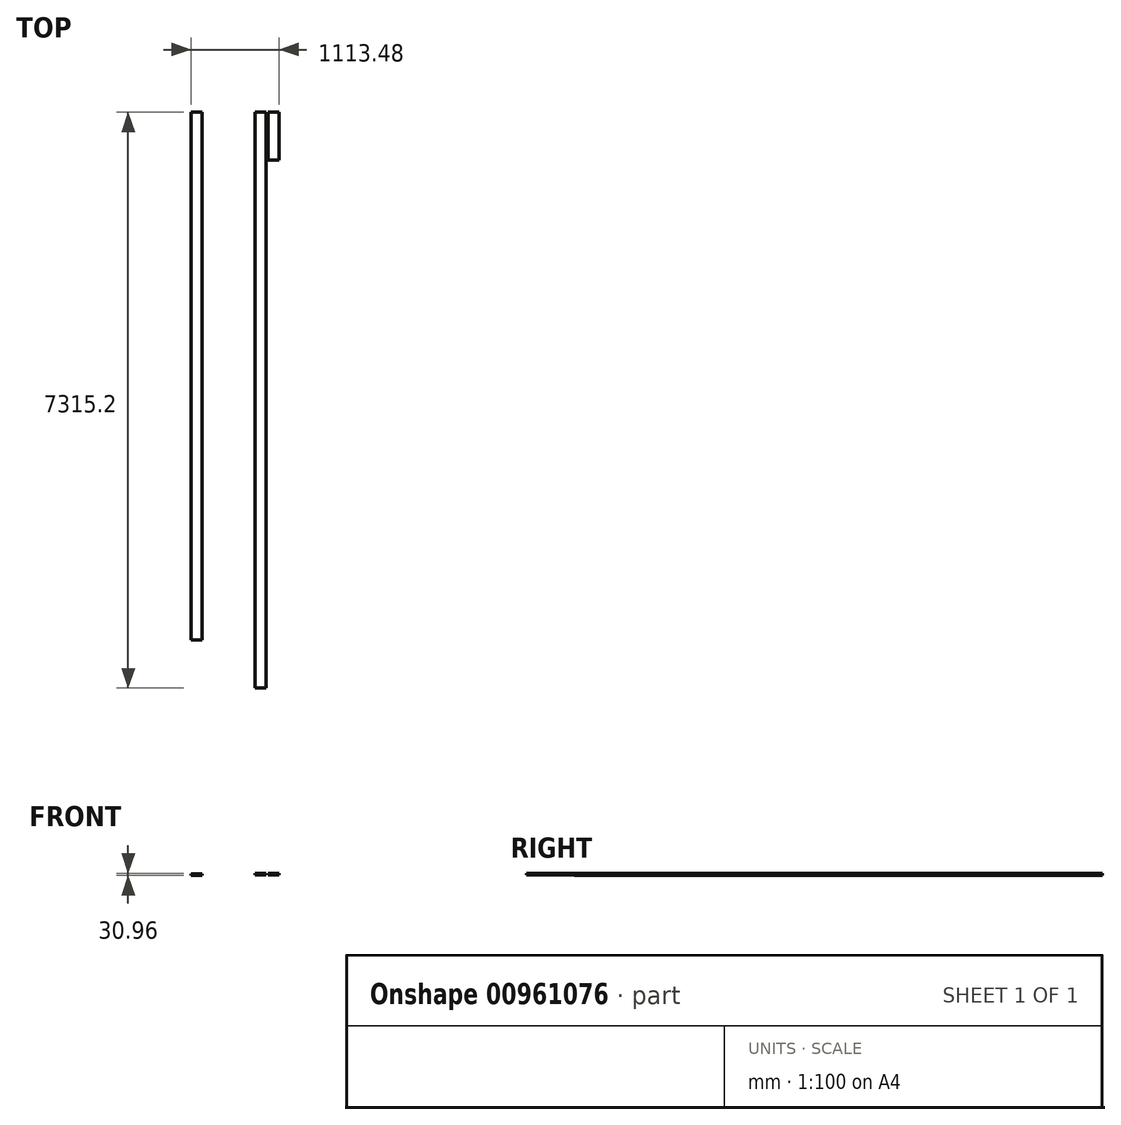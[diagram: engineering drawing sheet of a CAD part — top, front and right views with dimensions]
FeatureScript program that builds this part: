
annotation { "Feature Type Name" : "Feature", "Feature Type Description" : "" }
export const myFeature = defineFeature(function(context is Context, id is Id, definition is map)
    precondition{}
    {
        {
            var Q0;
            Q0=qCreatedBy(makeId("Front.planeOp"),FACE);
            var sketch = newSketch(context, id + "F0", { "sketchPlane" : qUnion([Q0])});
            skLineSegment(sketch, "E0.bottom", {"start": v(-146.06, 12.17) * mm, "end": v(-6.36, 12.17) * mm});
            skLineSegment(sketch, "E0.top", {"start": v(-146.06, -11.7) * mm, "end": v(-6.36, -11.7) * mm});
            skLineSegment(sketch, "E0.left", {"start": v(-146.06, 12.17) * mm, "end": v(-146.06, -11.7) * mm});
            skLineSegment(sketch, "E0.right", {"start": v(-6.36, 12.17) * mm, "end": v(-6.36, -11.7) * mm});
            skLineSegment(sketch, "E1.bottom", {"start": v(15.3, 12.22) * mm, "end": v(155, 12.22) * mm});
            skLineSegment(sketch, "E1.top", {"start": v(15.3, -11.66) * mm, "end": v(155, -11.66) * mm});
            skLineSegment(sketch, "E1.left", {"start": v(15.3, 12.22) * mm, "end": v(15.3, -11.66) * mm});
            skLineSegment(sketch, "E1.right", {"start": v(155, 12.22) * mm, "end": v(155, -11.66) * mm});
            skSolve(sketch);
        }
        {
            var Q0;
            Q0=qCreatedBy(makeId("Front.planeOp"),FACE);
            var sketch = newSketch(context, id + "F1", { "sketchPlane" : qUnion([Q0])});
            skLineSegment(sketch, "E2.bottom", {"start": v(-818.78, 4.12) * mm, "end": v(-958.48, 4.12) * mm});
            skLineSegment(sketch, "E2.top", {"start": v(-818.78, -18.74) * mm, "end": v(-958.48, -18.74) * mm});
            skLineSegment(sketch, "E2.left", {"start": v(-818.78, 4.12) * mm, "end": v(-818.78, -18.74) * mm});
            skLineSegment(sketch, "E2.right", {"start": v(-958.48, 4.12) * mm, "end": v(-958.48, -18.74) * mm});
            skPoint(sketch, "E2.middle", {"position": v(-888.63, -7.31) * mm});
            skLineSegment(sketch, "E3.1.0.0", {"start": v(-823.6, 4.12) * mm, "end": v(-823.6, -18.74) * mm});
            skLineSegment(sketch, "E3.1.0.1", {"start": v(-683.9, 4.12) * mm, "end": v(-823.6, 4.12) * mm});
            skLineSegment(sketch, "E3.1.0.2", {"start": v(-683.9, -18.74) * mm, "end": v(-823.6, -18.74) * mm});
            skLineSegment(sketch, "E3.1.0.3", {"start": v(-683.9, 4.12) * mm, "end": v(-683.9, -18.74) * mm});
            skLineSegment(sketch, "E3.2.0.0", {"start": v(-688.74, 4.12) * mm, "end": v(-688.74, -18.74) * mm});
            skLineSegment(sketch, "E3.2.0.1", {"start": v(-549.04, 4.12) * mm, "end": v(-688.74, 4.12) * mm});
            skLineSegment(sketch, "E3.2.0.2", {"start": v(-549.04, -18.74) * mm, "end": v(-688.74, -18.74) * mm});
            skLineSegment(sketch, "E3.2.0.3", {"start": v(-549.04, 4.12) * mm, "end": v(-549.04, -18.74) * mm});
            skLineSegment(sketch, "E3.3.0.0", {"start": v(-553.86, 4.12) * mm, "end": v(-553.86, -18.74) * mm});
            skLineSegment(sketch, "E3.3.0.1", {"start": v(-414.16, 4.12) * mm, "end": v(-553.86, 4.12) * mm});
            skLineSegment(sketch, "E3.3.0.2", {"start": v(-414.16, -18.74) * mm, "end": v(-553.86, -18.74) * mm});
            skLineSegment(sketch, "E3.3.0.3", {"start": v(-414.16, 4.12) * mm, "end": v(-414.16, -18.74) * mm});
            skLineSegment(sketch, "E3.4.0.0", {"start": v(-418.99, 4.12) * mm, "end": v(-418.99, -18.74) * mm});
            skLineSegment(sketch, "E3.4.0.1", {"start": v(-279.29, 4.12) * mm, "end": v(-418.99, 4.12) * mm});
            skLineSegment(sketch, "E3.4.0.2", {"start": v(-279.29, -18.74) * mm, "end": v(-418.99, -18.74) * mm});
            skLineSegment(sketch, "E3.4.0.3", {"start": v(-279.29, 4.12) * mm, "end": v(-279.29, -18.74) * mm});
            skLineSegment(sketch, "E3.5.0.0", {"start": v(-284.11, 4.12) * mm, "end": v(-284.11, -18.74) * mm});
            skLineSegment(sketch, "E3.5.0.1", {"start": v(-144.41, 4.12) * mm, "end": v(-284.11, 4.12) * mm});
            skLineSegment(sketch, "E3.5.0.2", {"start": v(-144.41, -18.74) * mm, "end": v(-284.11, -18.74) * mm});
            skLineSegment(sketch, "E3.5.0.3", {"start": v(-144.41, 4.12) * mm, "end": v(-144.41, -18.74) * mm});
            skLineSegment(sketch, "E3.direction1", {"start": v(-958.48, -18.74) * mm, "end": v(-823.6, -18.74) * mm, "construction": true});
            skLineSegment(sketch, "E4.0.6.0", {"start": v(-149.24, 4.12) * mm, "end": v(-149.24, -18.74) * mm});
            skLineSegment(sketch, "E4.3.6.0", {"start": v(-9.54, 4.12) * mm, "end": v(-149.24, 4.12) * mm});
            skLineSegment(sketch, "E4.6.6.0", {"start": v(-9.54, -18.74) * mm, "end": v(-149.24, -18.74) * mm});
            skLineSegment(sketch, "E4.9.6.0", {"start": v(-9.54, 4.12) * mm, "end": v(-9.54, -18.74) * mm});
            skLineSegment(sketch, "E4.0.7.0", {"start": v(-14.37, 4.12) * mm, "end": v(-14.37, -18.74) * mm});
            skLineSegment(sketch, "E4.3.7.0", {"start": v(125.33, 4.12) * mm, "end": v(-14.37, 4.12) * mm});
            skLineSegment(sketch, "E4.6.7.0", {"start": v(125.33, -18.74) * mm, "end": v(-14.37, -18.74) * mm});
            skLineSegment(sketch, "E4.9.7.0", {"start": v(125.33, 4.12) * mm, "end": v(125.33, -18.74) * mm});
            skLineSegment(sketch, "E4.0.8.0", {"start": v(120.5, 4.12) * mm, "end": v(120.5, -18.74) * mm});
            skLineSegment(sketch, "E4.3.8.0", {"start": v(260.2, 4.12) * mm, "end": v(120.5, 4.12) * mm});
            skLineSegment(sketch, "E4.6.8.0", {"start": v(260.2, -18.74) * mm, "end": v(120.5, -18.74) * mm});
            skLineSegment(sketch, "E4.9.8.0", {"start": v(260.2, 4.12) * mm, "end": v(260.2, -18.74) * mm});
            skLineSegment(sketch, "E4.0.9.0", {"start": v(255.38, 4.12) * mm, "end": v(255.38, -18.74) * mm});
            skLineSegment(sketch, "E4.3.9.0", {"start": v(395.08, 4.12) * mm, "end": v(255.38, 4.12) * mm});
            skLineSegment(sketch, "E4.6.9.0", {"start": v(395.08, -18.74) * mm, "end": v(255.38, -18.74) * mm});
            skLineSegment(sketch, "E4.9.9.0", {"start": v(395.08, 4.12) * mm, "end": v(395.08, -18.74) * mm});
            skLineSegment(sketch, "E5.0.10.0", {"start": v(390.26, 4.12) * mm, "end": v(390.26, -18.74) * mm});
            skLineSegment(sketch, "E5.3.10.0", {"start": v(529.96, 4.12) * mm, "end": v(390.26, 4.12) * mm});
            skLineSegment(sketch, "E5.6.10.0", {"start": v(529.96, -18.74) * mm, "end": v(390.26, -18.74) * mm});
            skLineSegment(sketch, "E5.9.10.0", {"start": v(529.96, 4.12) * mm, "end": v(529.96, -18.74) * mm});
            skLineSegment(sketch, "E5.0.11.0", {"start": v(525.13, 4.12) * mm, "end": v(525.13, -18.74) * mm});
            skLineSegment(sketch, "E5.3.11.0", {"start": v(664.83, 4.12) * mm, "end": v(525.13, 4.12) * mm});
            skLineSegment(sketch, "E5.6.11.0", {"start": v(664.83, -18.74) * mm, "end": v(525.13, -18.74) * mm});
            skLineSegment(sketch, "E5.9.11.0", {"start": v(664.83, 4.12) * mm, "end": v(664.83, -18.74) * mm});
            skLineSegment(sketch, "E5.0.12.0", {"start": v(660, 4.12) * mm, "end": v(660, -18.74) * mm});
            skLineSegment(sketch, "E5.3.12.0", {"start": v(799.7, 4.12) * mm, "end": v(660, 4.12) * mm});
            skLineSegment(sketch, "E5.6.12.0", {"start": v(799.7, -18.74) * mm, "end": v(660, -18.74) * mm});
            skLineSegment(sketch, "E5.9.12.0", {"start": v(799.7, 4.12) * mm, "end": v(799.7, -18.74) * mm});
            skLineSegment(sketch, "E5.0.13.0", {"start": v(794.88, 4.12) * mm, "end": v(794.88, -18.74) * mm});
            skLineSegment(sketch, "E5.3.13.0", {"start": v(934.58, 4.12) * mm, "end": v(794.88, 4.12) * mm});
            skLineSegment(sketch, "E5.6.13.0", {"start": v(934.58, -18.74) * mm, "end": v(794.88, -18.74) * mm});
            skLineSegment(sketch, "E5.9.13.0", {"start": v(934.58, 4.12) * mm, "end": v(934.58, -18.74) * mm});
            skLineSegment(sketch, "E5.0.14.0", {"start": v(929.75, 4.12) * mm, "end": v(929.75, -18.74) * mm});
            skLineSegment(sketch, "E5.3.14.0", {"start": v(1069.45, 4.12) * mm, "end": v(929.75, 4.12) * mm});
            skLineSegment(sketch, "E5.6.14.0", {"start": v(1069.45, -18.74) * mm, "end": v(929.75, -18.74) * mm});
            skLineSegment(sketch, "E5.9.14.0", {"start": v(1069.45, 4.12) * mm, "end": v(1069.45, -18.74) * mm});
            skSolve(sketch);
        }
        {
            var Q0;
            Q0=makeQuery(id+"F1.imprint","IMPRINT",FACE,{"disambiguationData":[TD([[makeQuery(id+"F1.imprint","IMPRINT",EDGE,{"derivedFrom":sQuery(id+"F1.wireOp",EDGE,"E2.bottom")}),1.0]])]});
            extrude(context, id + "F2", {"entities" : qUnion([Q0]), "depth" : 6705.6 * mm, "offsetDistance" : 25.4 * mm});
        }
        {
            var Q0;
            Q0=makeQuery(id+"F0.imprint","IMPRINT",FACE,{"disambiguationData":[TD([[makeQuery(id+"F0.imprint","IMPRINT",EDGE,{"derivedFrom":sQuery(id+"F0.wireOp",EDGE,"E0.bottom")}),-1.0]])]});
            extrude(context, id + "F3", {"entities" : qUnion([Q0]), "depth" : 7315.2 * mm, "offsetDistance" : 25.4 * mm});
        }
        {
            var Q0;
            Q0=makeQuery(id+"F0.imprint","IMPRINT",FACE,{"disambiguationData":[TD([[makeQuery(id+"F0.imprint","IMPRINT",EDGE,{"derivedFrom":sQuery(id+"F0.wireOp",EDGE,"E1.bottom")}),-1.0]])]});
            extrude(context, id + "F4", {"entities" : qUnion([Q0]), "depth" : 609.6 * mm, "offsetDistance" : 25.4 * mm});
        }
    });
